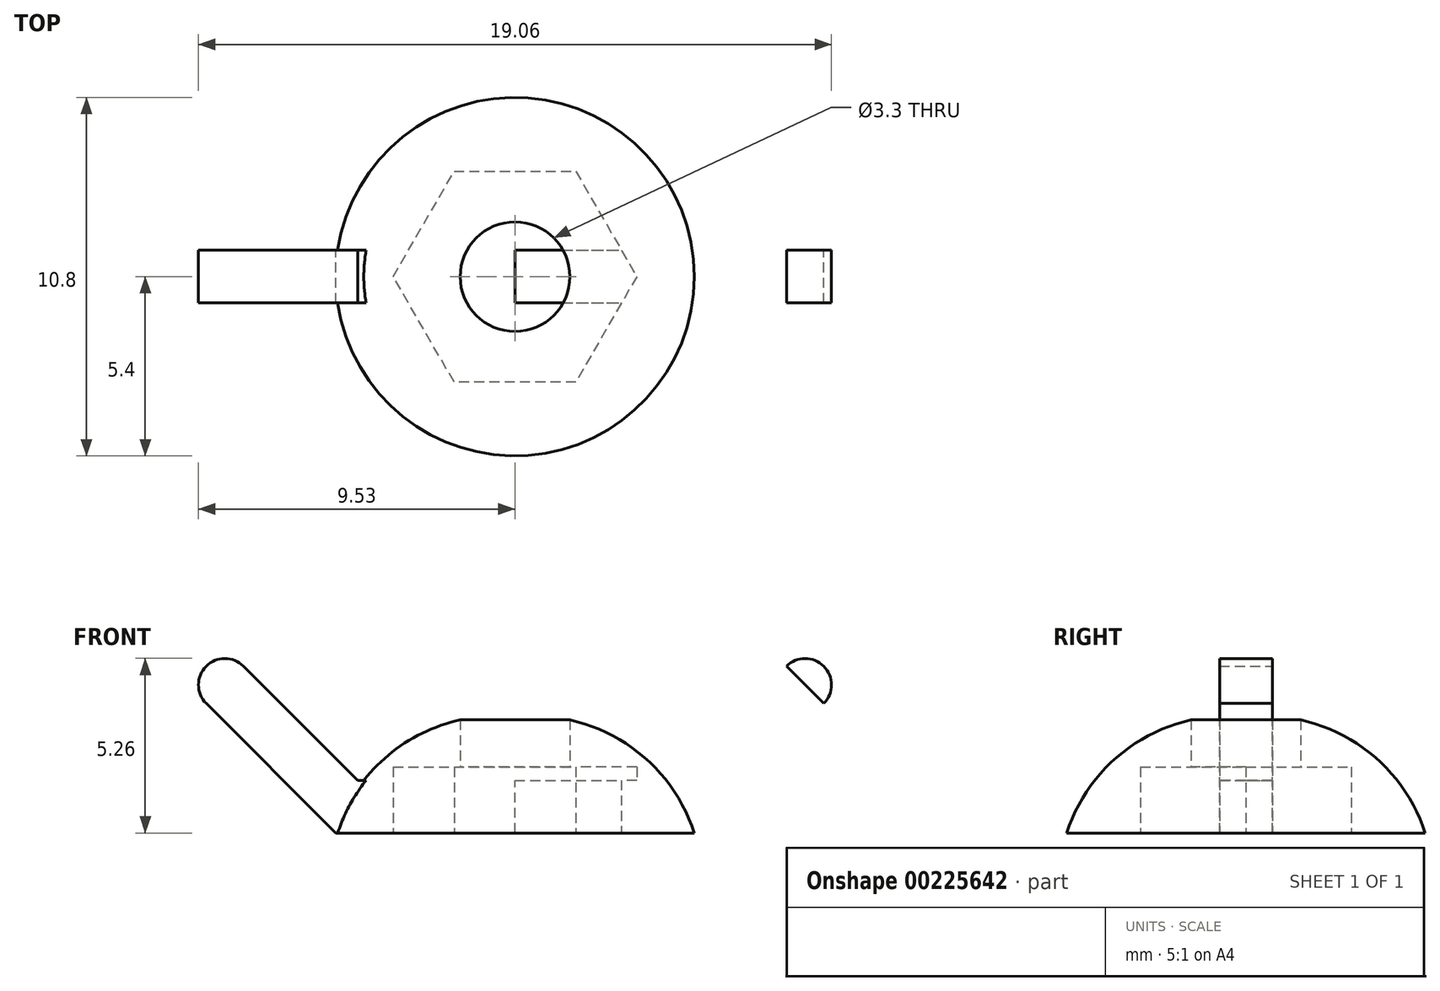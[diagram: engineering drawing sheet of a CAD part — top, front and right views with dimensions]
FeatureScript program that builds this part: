
annotation { "Feature Type Name" : "Feature", "Feature Type Description" : "" }
export const myFeature = defineFeature(function(context is Context, id is Id, definition is map)
    precondition{}
    {
        {
            var Q0;
            Q0=qCreatedBy(makeId("Top.planeOp"),FACE);
            var sketch = newSketch(context, id + "F0", { "sketchPlane" : qUnion([Q0])});
            skCircle(sketch, "E0.cCircle", {"center": v(0, 0) * mm, "radius": 3.18 * mm, "construction": true});
            skLineSegment(sketch, "E0.0", {"start": v(-1.83, 3.18) * mm, "end": v(1.83, 3.18) * mm});
            skLineSegment(sketch, "E0.1", {"start": v(1.83, 3.18) * mm, "end": v(3.67, 0) * mm});
            skLineSegment(sketch, "E0.2", {"start": v(3.67, 0) * mm, "end": v(1.83, -3.17) * mm});
            skLineSegment(sketch, "E0.3", {"start": v(1.83, -3.17) * mm, "end": v(-1.83, -3.18) * mm});
            skLineSegment(sketch, "E0.4", {"start": v(-1.83, -3.18) * mm, "end": v(-3.67, 0) * mm});
            skLineSegment(sketch, "E0.5", {"start": v(-3.67, 0) * mm, "end": v(-1.83, 3.17) * mm});
            skPoint(sketch, "E0.0.midPoint", {"position": v(0, 3.18) * mm});
            skCircle(sketch, "E1", {"center": v(0, 0) * mm, "radius": 1.65 * mm});
            skSolve(sketch);
        }
        {
            var Q0;
            Q0=qCreatedBy(makeId("Front.planeOp"),FACE);
            var sketch = newSketch(context, id + "F1", { "sketchPlane" : qUnion([Q0])});
            skLineSegment(sketch, "E2", {"start": v(0, 0) * mm, "end": v(3.81, 0) * mm});
            skLineSegment(sketch, "E3", {"start": v(0, 0) * mm, "end": v(0, 1.9) * mm});
            skLineSegment(sketch, "E4.top", {"start": v(0, 1.9) * mm, "end": v(3.81, 1.9) * mm});
            skLineSegment(sketch, "E4.right", {"start": v(3.81, 0) * mm, "end": v(3.81, 1.9) * mm});
            skLineSegment(sketch, "E5", {"start": v(3.81, 0) * mm, "end": v(5.4, 0) * mm});
            skLineSegment(sketch, "E6", {"start": v(0, 1.9) * mm, "end": v(0, 3.5) * mm});
            skArc(sketch, "E7", {"start": v(5.4, 0) * mm, "mid": v(3.32, 2.7) * mm, "end": v(0, 3.5) * mm});
            skSolve(sketch);
        }
        {
            var Q0;
            Q0=makeQuery(id+"F1.imprint","IMPRINT",FACE,{"disambiguationData":[TD([[makeQuery(id+"F1.imprint","IMPRINT",EDGE,{"derivedFrom":sQuery(id+"F1.wireOp",EDGE,"E4.top")}),1.0]])]});
            var Q1;
            Q1=makeQuery(id+"F1.imprint","IMPRINT",FACE,{"disambiguationData":[TD([[makeQuery(id+"F1.imprint","IMPRINT",EDGE,{"derivedFrom":sQuery(id+"F1.wireOp",EDGE,"E2")}),1.0]])]});
            var Q2;
            Q2=sQuery(id+"F1.wireOp",EDGE,"E6");
            revolve(context, id + "F2", {"entities" : qUnion([Q0, Q1]), "axis" : qUnion([Q2]), "revolveType" : RevolveType.FULL});
        }
        {
            var Q0;
            Q0=makeQuery(id+"F0.imprint","IMPRINT",FACE,{"disambiguationData":[TD([[makeQuery(id+"F0.imprint","IMPRINT",EDGE,{"derivedFrom":sQuery(id+"F0.wireOp",EDGE,"E0.0")}),-1.0]])]});
            extrude(context, id + "F3", {"entities" : qUnion([Q0]), "operationType" : NewBodyOperationType.REMOVE, "depth" : 1.98 * mm});
        }
        {
            var Q0;
            Q0=makeQuery(id+"F0.imprint","IMPRINT",FACE,{"disambiguationData":[TD([[makeQuery(id+"F0.imprint","IMPRINT",EDGE,{"derivedFrom":sQuery(id+"F0.wireOp",EDGE,"E1")}),1.0]])]});
            extrude(context, id + "F4", {"entities" : qUnion([Q0]), "operationType" : NewBodyOperationType.REMOVE, "depth" : 6.35 * mm});
        }
        {
            var Q0;
            Q0=qCreatedBy(makeId("Front.planeOp"),FACE);
            var sketch = newSketch(context, id + "F5", { "sketchPlane" : qUnion([Q0])});
            skLineSegment(sketch, "E8", {"start": v(0, 0) * mm, "end": v(5.4, 0) * mm});
            skLineSegment(sketch, "E9", {"start": v(5.4, 0) * mm, "end": v(9.3, 3.9) * mm});
            skLineSegment(sketch, "E10", {"start": v(0, 0) * mm, "end": v(0, 1.59) * mm});
            skLineSegment(sketch, "E11", {"start": v(9.3, 3.9) * mm, "end": v(8.18, 5.02) * mm});
            skLineSegment(sketch, "E12", {"start": v(8.18, 5.02) * mm, "end": v(4.74, 1.59) * mm});
            skLineSegment(sketch, "E13", {"start": v(0, 1.59) * mm, "end": v(4.74, 1.59) * mm});
            skLineSegment(sketch, "E14.MirrorCS", {"start": v(0, 1.59) * mm, "end": v(-4.74, 1.59) * mm});
            skLineSegment(sketch, "E15.MirrorCS", {"start": v(-8.18, 5.02) * mm, "end": v(-4.74, 1.59) * mm});
            skLineSegment(sketch, "E16.MirrorCS", {"start": v(-9.3, 3.9) * mm, "end": v(-8.18, 5.02) * mm});
            skLineSegment(sketch, "E17.MirrorCS", {"start": v(-5.4, 0) * mm, "end": v(-9.3, 3.9) * mm});
            skLineSegment(sketch, "E18.MirrorCS", {"start": v(0, 0) * mm, "end": v(-5.4, 0) * mm});
            skArc(sketch, "E19", {"start": v(-9.3, 3.9) * mm, "mid": v(-9.3, 5.02) * mm, "end": v(-8.18, 5.02) * mm});
            skArc(sketch, "E20", {"start": v(8.18, 5.02) * mm, "mid": v(9.3, 5.02) * mm, "end": v(9.3, 3.9) * mm});
            skLineSegment(sketch, "E21", {"start": v(0, 0) * mm, "end": v(3.81, 0) * mm});
            skLineSegment(sketch, "E22", {"start": v(3.81, 0) * mm, "end": v(3.81, 1.59) * mm});
            skLineSegment(sketch, "E23.MirrorCS", {"start": v(-3.81, 0) * mm, "end": v(-3.81, 1.59) * mm});
            skSolve(sketch);
        }
        {
            var Q0;
            {var subQ2=sQuery(id+"F5.wireOp",EDGE,"E15.MirrorCS");Q0=makeQuery(id+"F5.imprint","IMPRINT",FACE,{"disambiguationData":[TD([[makeQuery(id+"F5.imprint","IMPRINT",EDGE,{"derivedFrom":subQ2}),-1.0]])]});}
            var Q1;
            Q1=makeQuery(id+"F5.imprint","IMPRINT",FACE,{"disambiguationData":[TD([[makeQuery(id+"F5.imprint","IMPRINT",EDGE,{"derivedFrom":sQuery(id+"F5.wireOp",EDGE,"E16.MirrorCS")}),1.0]])]});
            var Q2;
            Q2=makeQuery(id+"F5.imprint","IMPRINT",FACE,{"disambiguationData":[TD([[makeQuery(id+"F5.imprint","IMPRINT",EDGE,{"derivedFrom":sQuery(id+"F5.wireOp",EDGE,"E8")}),1.0]])]});
            var Q3;
            Q3=makeQuery(id+"F5.imprint","IMPRINT",FACE,{"disambiguationData":[TD([[makeQuery(id+"F5.imprint","IMPRINT",EDGE,{"derivedFrom":sQuery(id+"F5.wireOp",EDGE,"E11")}),-1.0]])]});
            extrude(context, id + "F6", {"entities" : qUnion([Q0, Q1, Q2, Q3]), "operationType" : NewBodyOperationType.ADD, "endBound" : BoundingType.SYMMETRIC, "depth" : 1.59 * mm});
        }
    });
